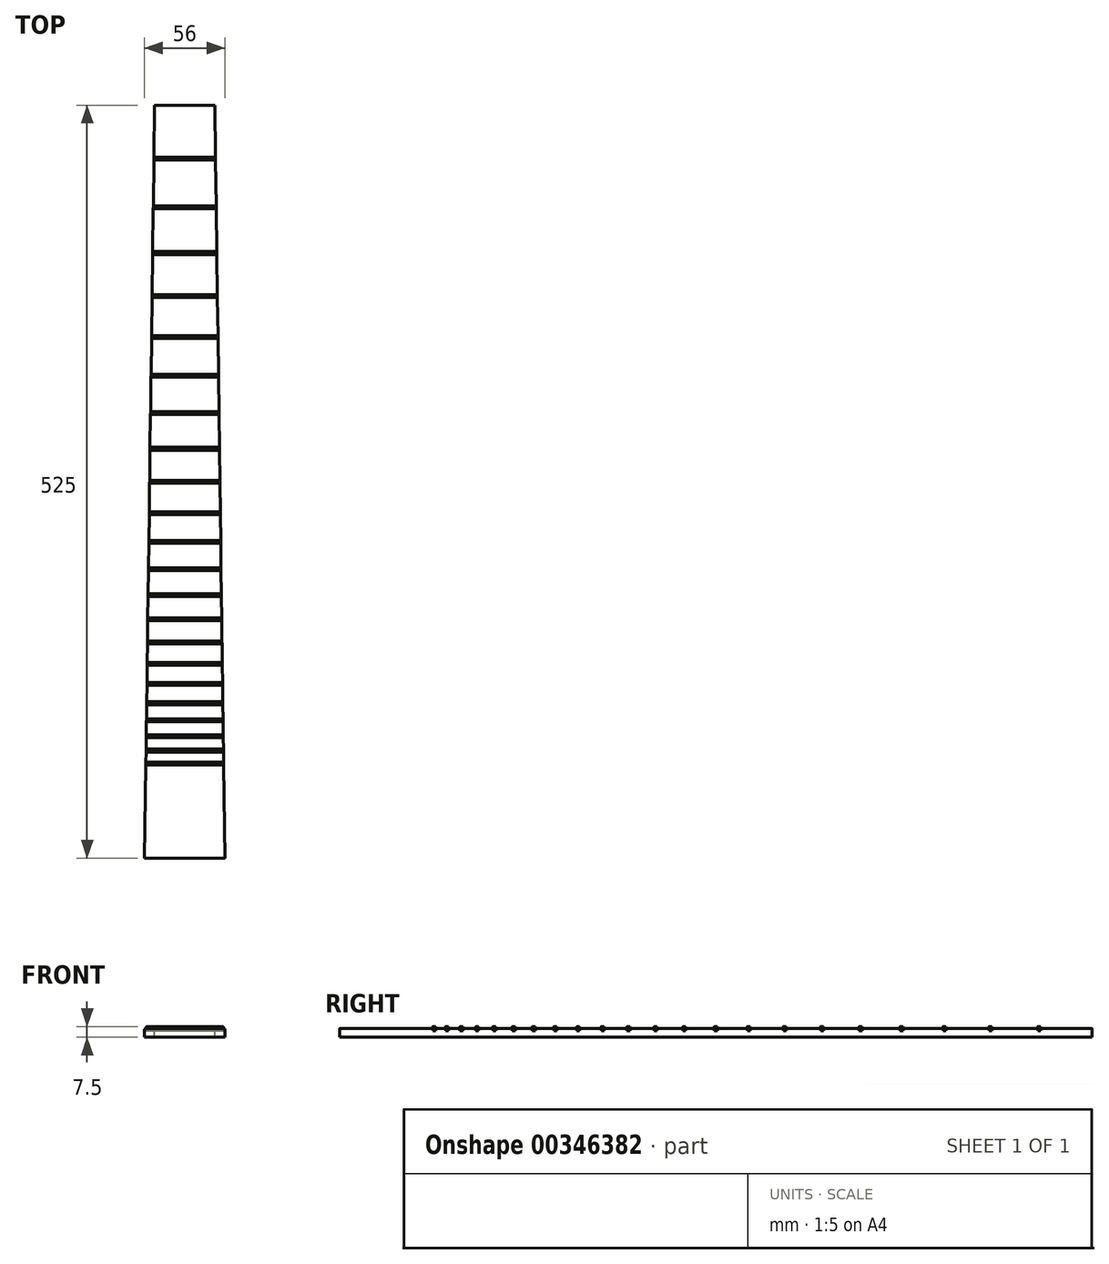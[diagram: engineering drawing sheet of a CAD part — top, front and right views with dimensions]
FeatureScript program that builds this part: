
annotation { "Feature Type Name" : "Feature", "Feature Type Description" : "" }
export const myFeature = defineFeature(function(context is Context, id is Id, definition is map)
    precondition{}
    {
        {
            var Q0;
            Q0=qCreatedBy(makeId("Top.planeOp"),FACE);
            var sketch = newSketch(context, id + "F0", { "sketchPlane" : qUnion([Q0])});
            skLineSegment(sketch, "E0", {"start": v(0, 0) * mm, "end": v(0, 525) * mm, "construction": true});
            skLineSegment(sketch, "E1", {"start": v(0, 525) * mm, "end": v(-21, 525) * mm});
            skLineSegment(sketch, "E2", {"start": v(0, 0) * mm, "end": v(-28, 0) * mm});
            skLineSegment(sketch, "E3", {"start": v(-28, 0) * mm, "end": v(-21, 525) * mm});
            skLineSegment(sketch, "E4", {"start": v(-21.48, 489) * mm, "end": v(0, 489) * mm});
            skLineSegment(sketch, "E5", {"start": v(-21.5, 487) * mm, "end": v(0, 487) * mm});
            skLineSegment(sketch, "E6", {"start": v(-21.93, 455) * mm, "end": v(0, 455) * mm});
            skLineSegment(sketch, "E7", {"start": v(-21.96, 453) * mm, "end": v(0, 453) * mm});
            skLineSegment(sketch, "E8", {"start": v(-22.36, 423) * mm, "end": v(0, 423) * mm});
            skLineSegment(sketch, "E9", {"start": v(-22.39, 421) * mm, "end": v(0, 421) * mm});
            skLineSegment(sketch, "E10", {"start": v(-22.76, 393) * mm, "end": v(0, 393) * mm});
            skLineSegment(sketch, "E11", {"start": v(-22.79, 391) * mm, "end": v(0, 391) * mm});
            skLineSegment(sketch, "E12", {"start": v(-23.14, 364.5) * mm, "end": v(0, 364.5) * mm});
            skLineSegment(sketch, "E13", {"start": v(-23.17, 362.5) * mm, "end": v(0, 362.5) * mm});
            skLineSegment(sketch, "E14", {"start": v(-23.5, 337.5) * mm, "end": v(0, 337.5) * mm});
            skLineSegment(sketch, "E15", {"start": v(-23.53, 335.5) * mm, "end": v(0, 335.5) * mm});
            skLineSegment(sketch, "E16", {"start": v(-23.85, 311.5) * mm, "end": v(0, 311.5) * mm});
            skLineSegment(sketch, "E17", {"start": v(-23.87, 309.5) * mm, "end": v(0, 309.5) * mm});
            skLineSegment(sketch, "E18", {"start": v(-24.18, 286.5) * mm, "end": v(0, 286.5) * mm});
            skLineSegment(sketch, "E19", {"start": v(-24.2, 284.5) * mm, "end": v(0, 284.5) * mm});
            skLineSegment(sketch, "E20", {"start": v(-24.49, 263.5) * mm, "end": v(0, 263.5) * mm});
            skLineSegment(sketch, "E21", {"start": v(-24.51, 261.5) * mm, "end": v(0, 261.5) * mm});
            skLineSegment(sketch, "E22", {"start": v(-24.78, 241.5) * mm, "end": v(0, 241.5) * mm});
            skLineSegment(sketch, "E23", {"start": v(-24.8, 239.5) * mm, "end": v(0, 239.5) * mm});
            skLineSegment(sketch, "E24", {"start": v(-25.05, 221.5) * mm, "end": v(0, 221.5) * mm});
            skLineSegment(sketch, "E25", {"start": v(-25.07, 219.5) * mm, "end": v(0, 219.5) * mm});
            skLineSegment(sketch, "E26", {"start": v(-25.3, 202.5) * mm, "end": v(0, 202.5) * mm});
            skLineSegment(sketch, "E27", {"start": v(-25.33, 200.5) * mm, "end": v(0, 200.5) * mm});
            skLineSegment(sketch, "E28", {"start": v(-25.54, 184.5) * mm, "end": v(0, 184.5) * mm});
            skLineSegment(sketch, "E29", {"start": v(-25.57, 182.5) * mm, "end": v(0, 182.5) * mm});
            skLineSegment(sketch, "E30", {"start": v(-25.77, 167.5) * mm, "end": v(0, 167.5) * mm});
            skLineSegment(sketch, "E31", {"start": v(-25.8, 165.5) * mm, "end": v(0, 165.5) * mm});
            skLineSegment(sketch, "E32", {"start": v(-25.98, 151.5) * mm, "end": v(0, 151.5) * mm});
            skLineSegment(sketch, "E33", {"start": v(-26, 149.5) * mm, "end": v(0, 149.5) * mm});
            skLineSegment(sketch, "E34", {"start": v(-26.18, 136.5) * mm, "end": v(0, 136.5) * mm});
            skLineSegment(sketch, "E35", {"start": v(-26.2, 134.5) * mm, "end": v(0, 134.5) * mm});
            skLineSegment(sketch, "E36", {"start": v(-26.37, 122.5) * mm, "end": v(0, 122.5) * mm});
            skLineSegment(sketch, "E37", {"start": v(-26.4, 120.5) * mm, "end": v(0, 120.5) * mm});
            skLineSegment(sketch, "E38", {"start": v(-26.55, 109) * mm, "end": v(0, 109) * mm});
            skLineSegment(sketch, "E39", {"start": v(-26.57, 107) * mm, "end": v(0, 107) * mm});
            skLineSegment(sketch, "E40", {"start": v(-26.7, 97) * mm, "end": v(0, 97) * mm});
            skLineSegment(sketch, "E41", {"start": v(-26.73, 95) * mm, "end": v(0, 95) * mm});
            skLineSegment(sketch, "E42", {"start": v(-26.85, 86) * mm, "end": v(0, 86) * mm});
            skLineSegment(sketch, "E43", {"start": v(-26.88, 84) * mm, "end": v(0, 84) * mm});
            skLineSegment(sketch, "E44", {"start": v(-26.99, 76) * mm, "end": v(0, 76) * mm});
            skLineSegment(sketch, "E45", {"start": v(-27.01, 74) * mm, "end": v(0, 74) * mm});
            skLineSegment(sketch, "E46", {"start": v(-27.1, 67) * mm, "end": v(0, 67) * mm});
            skLineSegment(sketch, "E47", {"start": v(-27.13, 65) * mm, "end": v(0, 65) * mm});
            skLineSegment(sketch, "E48.MirrorCS", {"start": v(21, 525) * mm, "end": v(0, 525) * mm});
            skLineSegment(sketch, "E49.MirrorCS", {"start": v(28, 0) * mm, "end": v(21, 525) * mm});
            skLineSegment(sketch, "E50.MirrorCS", {"start": v(21.48, 489) * mm, "end": v(0, 489) * mm});
            skLineSegment(sketch, "E51.MirrorCS", {"start": v(21.5, 487) * mm, "end": v(0, 487) * mm});
            skLineSegment(sketch, "E52.MirrorCS", {"start": v(21.93, 455) * mm, "end": v(0, 455) * mm});
            skLineSegment(sketch, "E53.MirrorCS", {"start": v(21.96, 453) * mm, "end": v(0, 453) * mm});
            skLineSegment(sketch, "E54.MirrorCS", {"start": v(22.36, 423) * mm, "end": v(0, 423) * mm});
            skLineSegment(sketch, "E55.MirrorCS", {"start": v(22.39, 421) * mm, "end": v(0, 421) * mm});
            skLineSegment(sketch, "E56.MirrorCS", {"start": v(22.76, 393) * mm, "end": v(0, 393) * mm});
            skLineSegment(sketch, "E57.MirrorCS", {"start": v(22.79, 391) * mm, "end": v(0, 391) * mm});
            skLineSegment(sketch, "E58.MirrorCS", {"start": v(23.14, 364.5) * mm, "end": v(0, 364.5) * mm});
            skLineSegment(sketch, "E59.MirrorCS", {"start": v(23.17, 362.5) * mm, "end": v(0, 362.5) * mm});
            skLineSegment(sketch, "E60.MirrorCS", {"start": v(23.5, 337.5) * mm, "end": v(0, 337.5) * mm});
            skLineSegment(sketch, "E61.MirrorCS", {"start": v(23.53, 335.5) * mm, "end": v(0, 335.5) * mm});
            skLineSegment(sketch, "E62.MirrorCS", {"start": v(23.85, 311.5) * mm, "end": v(0, 311.5) * mm});
            skLineSegment(sketch, "E63.MirrorCS", {"start": v(23.87, 309.5) * mm, "end": v(0, 309.5) * mm});
            skLineSegment(sketch, "E64.MirrorCS", {"start": v(24.18, 286.5) * mm, "end": v(0, 286.5) * mm});
            skLineSegment(sketch, "E65.MirrorCS", {"start": v(24.2, 284.5) * mm, "end": v(0, 284.5) * mm});
            skLineSegment(sketch, "E66.MirrorCS", {"start": v(24.49, 263.5) * mm, "end": v(0, 263.5) * mm});
            skLineSegment(sketch, "E67.MirrorCS", {"start": v(24.51, 261.5) * mm, "end": v(0, 261.5) * mm});
            skLineSegment(sketch, "E68.MirrorCS", {"start": v(24.78, 241.5) * mm, "end": v(0, 241.5) * mm});
            skLineSegment(sketch, "E69.MirrorCS", {"start": v(24.8, 239.5) * mm, "end": v(0, 239.5) * mm});
            skLineSegment(sketch, "E70.MirrorCS", {"start": v(25.05, 221.5) * mm, "end": v(0, 221.5) * mm});
            skLineSegment(sketch, "E71.MirrorCS", {"start": v(25.07, 219.5) * mm, "end": v(0, 219.5) * mm});
            skLineSegment(sketch, "E72.MirrorCS", {"start": v(25.3, 202.5) * mm, "end": v(0, 202.5) * mm});
            skLineSegment(sketch, "E73.MirrorCS", {"start": v(25.33, 200.5) * mm, "end": v(0, 200.5) * mm});
            skLineSegment(sketch, "E74.MirrorCS", {"start": v(25.54, 184.5) * mm, "end": v(0, 184.5) * mm});
            skLineSegment(sketch, "E75.MirrorCS", {"start": v(25.57, 182.5) * mm, "end": v(0, 182.5) * mm});
            skLineSegment(sketch, "E76.MirrorCS", {"start": v(25.77, 167.5) * mm, "end": v(0, 167.5) * mm});
            skLineSegment(sketch, "E77.MirrorCS", {"start": v(25.8, 165.5) * mm, "end": v(0, 165.5) * mm});
            skLineSegment(sketch, "E78.MirrorCS", {"start": v(25.98, 151.5) * mm, "end": v(0, 151.5) * mm});
            skLineSegment(sketch, "E79.MirrorCS", {"start": v(26, 149.5) * mm, "end": v(0, 149.5) * mm});
            skLineSegment(sketch, "E80.MirrorCS", {"start": v(26.18, 136.5) * mm, "end": v(0, 136.5) * mm});
            skLineSegment(sketch, "E81.MirrorCS", {"start": v(26.2, 134.5) * mm, "end": v(0, 134.5) * mm});
            skLineSegment(sketch, "E82.MirrorCS", {"start": v(26.37, 122.5) * mm, "end": v(0, 122.5) * mm});
            skLineSegment(sketch, "E83.MirrorCS", {"start": v(26.4, 120.5) * mm, "end": v(0, 120.5) * mm});
            skLineSegment(sketch, "E84.MirrorCS", {"start": v(26.55, 109) * mm, "end": v(0, 109) * mm});
            skLineSegment(sketch, "E85.MirrorCS", {"start": v(26.57, 107) * mm, "end": v(0, 107) * mm});
            skLineSegment(sketch, "E86.MirrorCS", {"start": v(26.7, 97) * mm, "end": v(0, 97) * mm});
            skLineSegment(sketch, "E87.MirrorCS", {"start": v(26.73, 95) * mm, "end": v(0, 95) * mm});
            skLineSegment(sketch, "E88.MirrorCS", {"start": v(26.85, 86) * mm, "end": v(0, 86) * mm});
            skLineSegment(sketch, "E89.MirrorCS", {"start": v(26.88, 84) * mm, "end": v(0, 84) * mm});
            skLineSegment(sketch, "E90.MirrorCS", {"start": v(26.99, 76) * mm, "end": v(0, 76) * mm});
            skLineSegment(sketch, "E91.MirrorCS", {"start": v(27.01, 74) * mm, "end": v(0, 74) * mm});
            skLineSegment(sketch, "E92.MirrorCS", {"start": v(0, 0) * mm, "end": v(28, 0) * mm});
            skLineSegment(sketch, "E93.MirrorCS", {"start": v(27.1, 67) * mm, "end": v(0, 67) * mm});
            skLineSegment(sketch, "E94.MirrorCS", {"start": v(27.13, 65) * mm, "end": v(0, 65) * mm});
            skSolve(sketch);
        }
        {
            var Q0;
            Q0=qSketchRegion(id+"F0",true);
            extrude(context, id + "F1", {"entities" : qUnion([Q0]), "oppositeDirection" : true, "depth" : 6 * mm});
        }
        {
            var Q0;
            {var subQ1=sQuery(id+"F0.wireOp",EDGE,"E4");Q0=makeQuery(id+"F0.imprint","IMPRINT",FACE,{"disambiguationData":[TD([[makeQuery(id+"F0.imprint","IMPRINT",EDGE,{"derivedFrom":subQ1}),-1.0]])]});}
            var Q1;
            {var subQ1=sQuery(id+"F0.wireOp",EDGE,"E6");Q1=makeQuery(id+"F0.imprint","IMPRINT",FACE,{"disambiguationData":[TD([[makeQuery(id+"F0.imprint","IMPRINT",EDGE,{"derivedFrom":subQ1}),-1.0]])]});}
            var Q2;
            {var subQ1=sQuery(id+"F0.wireOp",EDGE,"E8");Q2=makeQuery(id+"F0.imprint","IMPRINT",FACE,{"disambiguationData":[TD([[makeQuery(id+"F0.imprint","IMPRINT",EDGE,{"derivedFrom":subQ1}),-1.0]])]});}
            var Q3;
            {var subQ0=sQuery(id+"F0.wireOp",EDGE,"E10");Q3=makeQuery(id+"F0.imprint","IMPRINT",FACE,{"disambiguationData":[TD([[makeQuery(id+"F0.imprint","IMPRINT",EDGE,{"derivedFrom":subQ0}),-1.0]])]});}
            var Q4;
            {var subQ1=sQuery(id+"F0.wireOp",EDGE,"E12");Q4=makeQuery(id+"F0.imprint","IMPRINT",FACE,{"disambiguationData":[TD([[makeQuery(id+"F0.imprint","IMPRINT",EDGE,{"derivedFrom":subQ1}),-1.0]])]});}
            var Q5;
            {var subQ1=sQuery(id+"F0.wireOp",EDGE,"E14");Q5=makeQuery(id+"F0.imprint","IMPRINT",FACE,{"disambiguationData":[TD([[makeQuery(id+"F0.imprint","IMPRINT",EDGE,{"derivedFrom":subQ1}),-1.0]])]});}
            var Q6;
            {var subQ1=sQuery(id+"F0.wireOp",EDGE,"E16");Q6=makeQuery(id+"F0.imprint","IMPRINT",FACE,{"disambiguationData":[TD([[makeQuery(id+"F0.imprint","IMPRINT",EDGE,{"derivedFrom":subQ1}),-1.0]])]});}
            var Q7;
            {var subQ4=sQuery(id+"F0.wireOp",EDGE,"E18");Q7=makeQuery(id+"F0.imprint","IMPRINT",FACE,{"disambiguationData":[TD([[makeQuery(id+"F0.imprint","IMPRINT",EDGE,{"derivedFrom":subQ4}),-1.0]])]});}
            var Q8;
            {var subQ0=sQuery(id+"F0.wireOp",EDGE,"E20");Q8=makeQuery(id+"F0.imprint","IMPRINT",FACE,{"disambiguationData":[TD([[makeQuery(id+"F0.imprint","IMPRINT",EDGE,{"derivedFrom":subQ0}),-1.0]])]});}
            var Q9;
            {var subQ1=sQuery(id+"F0.wireOp",EDGE,"E22");Q9=makeQuery(id+"F0.imprint","IMPRINT",FACE,{"disambiguationData":[TD([[makeQuery(id+"F0.imprint","IMPRINT",EDGE,{"derivedFrom":subQ1}),-1.0]])]});}
            var Q10;
            {var subQ1=sQuery(id+"F0.wireOp",EDGE,"E24");Q10=makeQuery(id+"F0.imprint","IMPRINT",FACE,{"disambiguationData":[TD([[makeQuery(id+"F0.imprint","IMPRINT",EDGE,{"derivedFrom":subQ1}),-1.0]])]});}
            var Q11;
            {var subQ1=sQuery(id+"F0.wireOp",EDGE,"E26");Q11=makeQuery(id+"F0.imprint","IMPRINT",FACE,{"disambiguationData":[TD([[makeQuery(id+"F0.imprint","IMPRINT",EDGE,{"derivedFrom":subQ1}),-1.0]])]});}
            var Q12;
            {var subQ4=sQuery(id+"F0.wireOp",EDGE,"E28");Q12=makeQuery(id+"F0.imprint","IMPRINT",FACE,{"disambiguationData":[TD([[makeQuery(id+"F0.imprint","IMPRINT",EDGE,{"derivedFrom":subQ4}),-1.0]])]});}
            var Q13;
            {var subQ0=sQuery(id+"F0.wireOp",EDGE,"E30");Q13=makeQuery(id+"F0.imprint","IMPRINT",FACE,{"disambiguationData":[TD([[makeQuery(id+"F0.imprint","IMPRINT",EDGE,{"derivedFrom":subQ0}),-1.0]])]});}
            var Q14;
            {var subQ1=sQuery(id+"F0.wireOp",EDGE,"E32");Q14=makeQuery(id+"F0.imprint","IMPRINT",FACE,{"disambiguationData":[TD([[makeQuery(id+"F0.imprint","IMPRINT",EDGE,{"derivedFrom":subQ1}),-1.0]])]});}
            var Q15;
            {var subQ1=sQuery(id+"F0.wireOp",EDGE,"E34");Q15=makeQuery(id+"F0.imprint","IMPRINT",FACE,{"disambiguationData":[TD([[makeQuery(id+"F0.imprint","IMPRINT",EDGE,{"derivedFrom":subQ1}),-1.0]])]});}
            var Q16;
            {var subQ1=sQuery(id+"F0.wireOp",EDGE,"E36");Q16=makeQuery(id+"F0.imprint","IMPRINT",FACE,{"disambiguationData":[TD([[makeQuery(id+"F0.imprint","IMPRINT",EDGE,{"derivedFrom":subQ1}),-1.0]])]});}
            var Q17;
            {var subQ4=sQuery(id+"F0.wireOp",EDGE,"E38");Q17=makeQuery(id+"F0.imprint","IMPRINT",FACE,{"disambiguationData":[TD([[makeQuery(id+"F0.imprint","IMPRINT",EDGE,{"derivedFrom":subQ4}),-1.0]])]});}
            var Q18;
            {var subQ0=sQuery(id+"F0.wireOp",EDGE,"E40");Q18=makeQuery(id+"F0.imprint","IMPRINT",FACE,{"disambiguationData":[TD([[makeQuery(id+"F0.imprint","IMPRINT",EDGE,{"derivedFrom":subQ0}),-1.0]])]});}
            var Q19;
            {var subQ1=sQuery(id+"F0.wireOp",EDGE,"E46");Q19=makeQuery(id+"F0.imprint","IMPRINT",FACE,{"disambiguationData":[TD([[makeQuery(id+"F0.imprint","IMPRINT",EDGE,{"derivedFrom":subQ1}),-1.0]])]});}
            var Q20;
            {var subQ1=sQuery(id+"F0.wireOp",EDGE,"E44");Q20=makeQuery(id+"F0.imprint","IMPRINT",FACE,{"disambiguationData":[TD([[makeQuery(id+"F0.imprint","IMPRINT",EDGE,{"derivedFrom":subQ1}),-1.0]])]});}
            var Q21;
            {var subQ4=sQuery(id+"F0.wireOp",EDGE,"E42");Q21=makeQuery(id+"F0.imprint","IMPRINT",FACE,{"disambiguationData":[TD([[makeQuery(id+"F0.imprint","IMPRINT",EDGE,{"derivedFrom":subQ4}),-1.0]])]});}
            extrude(context, id + "F2", {"entities" : qUnion([Q0, Q1, Q2, Q3, Q4, Q5, Q6, Q7, Q8, Q9, Q10, Q11, Q12, Q13, Q14, Q15, Q16, Q17, Q18, Q19, Q20, Q21]), "endBound" : BoundingType.SYMMETRIC, "depth" : 3 * mm});
        }
        {
            var Q0;
            Q0=makeQuery(id+"F1.opExtrude","CAP_EDGE",EDGE,{"disambiguationData":[OSD([sQuery(id+"F0.wireOp",EDGE,"E3")])],"isStart":true});
            var Q1;
            Q1=makeQuery(id+"F1.opExtrude","CAP_EDGE",EDGE,{"disambiguationData":[OSD([sQuery(id+"F0.wireOp",EDGE,"E49.MirrorCS")])],"isStart":true});
            fillet(context, id + "F3", {"entities" : qUnion([Q0, Q1]), "radius" : 0.5 * mm, "tangentPropagation" : true, "allowEdgeOverflow" : false});
        }
        {
            var Q0;
            Q0=makeQuery(id+"F2.opExtrude","SWEPT_BODY",BODY,{"disambiguationData":[OSD([sQuery(id+"F0.wireOp",EDGE,"E3"),sQuery(id+"F0.wireOp",EDGE,"E46"),sQuery(id+"F0.wireOp",EDGE,"E47"),sQuery(id+"F0.wireOp",EDGE,"E49.MirrorCS"),sQuery(id+"F0.wireOp",EDGE,"E93.MirrorCS"),sQuery(id+"F0.wireOp",EDGE,"E94.MirrorCS")])]});
            var Q1;
            Q1=makeQuery(id+"F2.opExtrude","SWEPT_BODY",BODY,{"disambiguationData":[OSD([sQuery(id+"F0.wireOp",EDGE,"E3"),sQuery(id+"F0.wireOp",EDGE,"E44"),sQuery(id+"F0.wireOp",EDGE,"E45"),sQuery(id+"F0.wireOp",EDGE,"E49.MirrorCS"),sQuery(id+"F0.wireOp",EDGE,"E90.MirrorCS"),sQuery(id+"F0.wireOp",EDGE,"E91.MirrorCS")])]});
            var Q2;
            Q2=makeQuery(id+"F2.opExtrude","SWEPT_BODY",BODY,{"disambiguationData":[OSD([sQuery(id+"F0.wireOp",EDGE,"E3"),sQuery(id+"F0.wireOp",EDGE,"E42"),sQuery(id+"F0.wireOp",EDGE,"E43"),sQuery(id+"F0.wireOp",EDGE,"E49.MirrorCS"),sQuery(id+"F0.wireOp",EDGE,"E88.MirrorCS"),sQuery(id+"F0.wireOp",EDGE,"E89.MirrorCS")])]});
            var Q3;
            Q3=makeQuery(id+"F2.opExtrude","SWEPT_BODY",BODY,{"disambiguationData":[OSD([sQuery(id+"F0.wireOp",EDGE,"E3"),sQuery(id+"F0.wireOp",EDGE,"E40"),sQuery(id+"F0.wireOp",EDGE,"E41"),sQuery(id+"F0.wireOp",EDGE,"E49.MirrorCS"),sQuery(id+"F0.wireOp",EDGE,"E86.MirrorCS"),sQuery(id+"F0.wireOp",EDGE,"E87.MirrorCS")])]});
            var Q4;
            Q4=makeQuery(id+"F2.opExtrude","SWEPT_BODY",BODY,{"disambiguationData":[OSD([sQuery(id+"F0.wireOp",EDGE,"E3"),sQuery(id+"F0.wireOp",EDGE,"E38"),sQuery(id+"F0.wireOp",EDGE,"E39"),sQuery(id+"F0.wireOp",EDGE,"E49.MirrorCS"),sQuery(id+"F0.wireOp",EDGE,"E84.MirrorCS"),sQuery(id+"F0.wireOp",EDGE,"E85.MirrorCS")])]});
            var Q5;
            Q5=makeQuery(id+"F2.opExtrude","SWEPT_BODY",BODY,{"disambiguationData":[OSD([sQuery(id+"F0.wireOp",EDGE,"E3"),sQuery(id+"F0.wireOp",EDGE,"E36"),sQuery(id+"F0.wireOp",EDGE,"E37"),sQuery(id+"F0.wireOp",EDGE,"E49.MirrorCS"),sQuery(id+"F0.wireOp",EDGE,"E82.MirrorCS"),sQuery(id+"F0.wireOp",EDGE,"E83.MirrorCS")])]});
            var Q6;
            Q6=makeQuery(id+"F2.opExtrude","SWEPT_BODY",BODY,{"disambiguationData":[OSD([sQuery(id+"F0.wireOp",EDGE,"E3"),sQuery(id+"F0.wireOp",EDGE,"E34"),sQuery(id+"F0.wireOp",EDGE,"E35"),sQuery(id+"F0.wireOp",EDGE,"E49.MirrorCS"),sQuery(id+"F0.wireOp",EDGE,"E80.MirrorCS"),sQuery(id+"F0.wireOp",EDGE,"E81.MirrorCS")])]});
            var Q7;
            Q7=makeQuery(id+"F2.opExtrude","SWEPT_BODY",BODY,{"disambiguationData":[OSD([sQuery(id+"F0.wireOp",EDGE,"E3"),sQuery(id+"F0.wireOp",EDGE,"E32"),sQuery(id+"F0.wireOp",EDGE,"E33"),sQuery(id+"F0.wireOp",EDGE,"E49.MirrorCS"),sQuery(id+"F0.wireOp",EDGE,"E78.MirrorCS"),sQuery(id+"F0.wireOp",EDGE,"E79.MirrorCS")])]});
            var Q8;
            Q8=makeQuery(id+"F2.opExtrude","SWEPT_BODY",BODY,{"disambiguationData":[OSD([sQuery(id+"F0.wireOp",EDGE,"E3"),sQuery(id+"F0.wireOp",EDGE,"E30"),sQuery(id+"F0.wireOp",EDGE,"E31"),sQuery(id+"F0.wireOp",EDGE,"E49.MirrorCS"),sQuery(id+"F0.wireOp",EDGE,"E76.MirrorCS"),sQuery(id+"F0.wireOp",EDGE,"E77.MirrorCS")])]});
            var Q9;
            Q9=makeQuery(id+"F2.opExtrude","SWEPT_BODY",BODY,{"disambiguationData":[OSD([sQuery(id+"F0.wireOp",EDGE,"E3"),sQuery(id+"F0.wireOp",EDGE,"E28"),sQuery(id+"F0.wireOp",EDGE,"E29"),sQuery(id+"F0.wireOp",EDGE,"E49.MirrorCS"),sQuery(id+"F0.wireOp",EDGE,"E74.MirrorCS"),sQuery(id+"F0.wireOp",EDGE,"E75.MirrorCS")])]});
            var Q10;
            Q10=makeQuery(id+"F2.opExtrude","SWEPT_BODY",BODY,{"disambiguationData":[OSD([sQuery(id+"F0.wireOp",EDGE,"E3"),sQuery(id+"F0.wireOp",EDGE,"E26"),sQuery(id+"F0.wireOp",EDGE,"E27"),sQuery(id+"F0.wireOp",EDGE,"E49.MirrorCS"),sQuery(id+"F0.wireOp",EDGE,"E72.MirrorCS"),sQuery(id+"F0.wireOp",EDGE,"E73.MirrorCS")])]});
            var Q11;
            Q11=makeQuery(id+"F2.opExtrude","SWEPT_BODY",BODY,{"disambiguationData":[OSD([sQuery(id+"F0.wireOp",EDGE,"E3"),sQuery(id+"F0.wireOp",EDGE,"E24"),sQuery(id+"F0.wireOp",EDGE,"E25"),sQuery(id+"F0.wireOp",EDGE,"E49.MirrorCS"),sQuery(id+"F0.wireOp",EDGE,"E70.MirrorCS"),sQuery(id+"F0.wireOp",EDGE,"E71.MirrorCS")])]});
            var Q12;
            Q12=makeQuery(id+"F2.opExtrude","SWEPT_BODY",BODY,{"disambiguationData":[OSD([sQuery(id+"F0.wireOp",EDGE,"E3"),sQuery(id+"F0.wireOp",EDGE,"E22"),sQuery(id+"F0.wireOp",EDGE,"E23"),sQuery(id+"F0.wireOp",EDGE,"E49.MirrorCS"),sQuery(id+"F0.wireOp",EDGE,"E68.MirrorCS"),sQuery(id+"F0.wireOp",EDGE,"E69.MirrorCS")])]});
            var Q13;
            Q13=makeQuery(id+"F2.opExtrude","SWEPT_BODY",BODY,{"disambiguationData":[OSD([sQuery(id+"F0.wireOp",EDGE,"E3"),sQuery(id+"F0.wireOp",EDGE,"E20"),sQuery(id+"F0.wireOp",EDGE,"E21"),sQuery(id+"F0.wireOp",EDGE,"E49.MirrorCS"),sQuery(id+"F0.wireOp",EDGE,"E66.MirrorCS"),sQuery(id+"F0.wireOp",EDGE,"E67.MirrorCS")])]});
            var Q14;
            Q14=makeQuery(id+"F2.opExtrude","SWEPT_BODY",BODY,{"disambiguationData":[OSD([sQuery(id+"F0.wireOp",EDGE,"E3"),sQuery(id+"F0.wireOp",EDGE,"E18"),sQuery(id+"F0.wireOp",EDGE,"E19"),sQuery(id+"F0.wireOp",EDGE,"E49.MirrorCS"),sQuery(id+"F0.wireOp",EDGE,"E64.MirrorCS"),sQuery(id+"F0.wireOp",EDGE,"E65.MirrorCS")])]});
            var Q15;
            Q15=makeQuery(id+"F2.opExtrude","SWEPT_BODY",BODY,{"disambiguationData":[OSD([sQuery(id+"F0.wireOp",EDGE,"E3"),sQuery(id+"F0.wireOp",EDGE,"E16"),sQuery(id+"F0.wireOp",EDGE,"E17"),sQuery(id+"F0.wireOp",EDGE,"E49.MirrorCS"),sQuery(id+"F0.wireOp",EDGE,"E62.MirrorCS"),sQuery(id+"F0.wireOp",EDGE,"E63.MirrorCS")])]});
            var Q16;
            Q16=makeQuery(id+"F2.opExtrude","SWEPT_BODY",BODY,{"disambiguationData":[OSD([sQuery(id+"F0.wireOp",EDGE,"E3"),sQuery(id+"F0.wireOp",EDGE,"E14"),sQuery(id+"F0.wireOp",EDGE,"E15"),sQuery(id+"F0.wireOp",EDGE,"E49.MirrorCS"),sQuery(id+"F0.wireOp",EDGE,"E60.MirrorCS"),sQuery(id+"F0.wireOp",EDGE,"E61.MirrorCS")])]});
            var Q17;
            Q17=makeQuery(id+"F2.opExtrude","SWEPT_BODY",BODY,{"disambiguationData":[OSD([sQuery(id+"F0.wireOp",EDGE,"E3"),sQuery(id+"F0.wireOp",EDGE,"E12"),sQuery(id+"F0.wireOp",EDGE,"E13"),sQuery(id+"F0.wireOp",EDGE,"E49.MirrorCS"),sQuery(id+"F0.wireOp",EDGE,"E58.MirrorCS"),sQuery(id+"F0.wireOp",EDGE,"E59.MirrorCS")])]});
            var Q18;
            Q18=makeQuery(id+"F2.opExtrude","SWEPT_BODY",BODY,{"disambiguationData":[OSD([sQuery(id+"F0.wireOp",EDGE,"E3"),sQuery(id+"F0.wireOp",EDGE,"E10"),sQuery(id+"F0.wireOp",EDGE,"E11"),sQuery(id+"F0.wireOp",EDGE,"E49.MirrorCS"),sQuery(id+"F0.wireOp",EDGE,"E56.MirrorCS"),sQuery(id+"F0.wireOp",EDGE,"E57.MirrorCS")])]});
            var Q19;
            Q19=makeQuery(id+"F2.opExtrude","SWEPT_BODY",BODY,{"disambiguationData":[OSD([sQuery(id+"F0.wireOp",EDGE,"E3"),sQuery(id+"F0.wireOp",EDGE,"E8"),sQuery(id+"F0.wireOp",EDGE,"E9"),sQuery(id+"F0.wireOp",EDGE,"E49.MirrorCS"),sQuery(id+"F0.wireOp",EDGE,"E54.MirrorCS"),sQuery(id+"F0.wireOp",EDGE,"E55.MirrorCS")])]});
            var Q20;
            Q20=makeQuery(id+"F2.opExtrude","SWEPT_BODY",BODY,{"disambiguationData":[OSD([sQuery(id+"F0.wireOp",EDGE,"E3"),sQuery(id+"F0.wireOp",EDGE,"E6"),sQuery(id+"F0.wireOp",EDGE,"E7"),sQuery(id+"F0.wireOp",EDGE,"E49.MirrorCS"),sQuery(id+"F0.wireOp",EDGE,"E52.MirrorCS"),sQuery(id+"F0.wireOp",EDGE,"E53.MirrorCS")])]});
            var Q21;
            Q21=makeQuery(id+"F2.opExtrude","SWEPT_BODY",BODY,{"disambiguationData":[OSD([sQuery(id+"F0.wireOp",EDGE,"E3"),sQuery(id+"F0.wireOp",EDGE,"E4"),sQuery(id+"F0.wireOp",EDGE,"E5"),sQuery(id+"F0.wireOp",EDGE,"E49.MirrorCS"),sQuery(id+"F0.wireOp",EDGE,"E50.MirrorCS"),sQuery(id+"F0.wireOp",EDGE,"E51.MirrorCS")])]});
            var Q22;
            Q22=makeQuery(id+"F1.opExtrude","SWEPT_BODY",BODY,{"disambiguationData":[OSD([sQuery(id+"F0.wireOp",EDGE,"E1"),sQuery(id+"F0.wireOp",EDGE,"E2"),sQuery(id+"F0.wireOp",EDGE,"E3"),sQuery(id+"F0.wireOp",EDGE,"E48.MirrorCS"),sQuery(id+"F0.wireOp",EDGE,"E49.MirrorCS"),sQuery(id+"F0.wireOp",EDGE,"E92.MirrorCS")])]});
            booleanBodies(context, id + "F4", {"operationType" : BooleanOperationType.SUBTRACTION, "tools" : qUnion([Q0, Q1, Q2, Q3, Q4, Q5, Q6, Q7, Q8, Q9, Q10, Q11, Q12, Q13, Q14, Q15, Q16, Q17, Q18, Q19, Q20, Q21]), "targets" : qUnion([Q22]), "keepTools" : true});
        }
        {
            var Q0;
            {var subQ0=sQuery(id+"F0.wireOp",EDGE,"E3");Q0=makeQuery(id+"F2.opExtrude","CAP_EDGE",EDGE,{"disambiguationData":[OSD([subQ0]),TDD([makeQuery(id+"F0.imprint","IMPRINT",EDGE,{"disambiguationData":[TD([[makeQuery(id+"F0.imprint","INTERSECT",VERTEX,{"derivedFrom":[subQ0,sQuery(id+"F0.wireOp",EDGE,"E4")]}),1.0]])],"derivedFrom":subQ0})])],"isStart":false});}
            var Q1;
            {var subQ0=sQuery(id+"F0.wireOp",EDGE,"E49.MirrorCS");Q1=makeQuery(id+"F2.opExtrude","CAP_EDGE",EDGE,{"disambiguationData":[OSD([subQ0]),TDD([makeQuery(id+"F0.imprint","IMPRINT",EDGE,{"disambiguationData":[TD([[makeQuery(id+"F0.imprint","INTERSECT",VERTEX,{"derivedFrom":[subQ0,sQuery(id+"F0.wireOp",EDGE,"E50.MirrorCS")]}),1.0]])],"derivedFrom":subQ0})])],"isStart":false});}
            var Q2;
            {var subQ0=sQuery(id+"F0.wireOp",EDGE,"E49.MirrorCS");Q2=makeQuery(id+"F2.opExtrude","CAP_EDGE",EDGE,{"disambiguationData":[OSD([subQ0]),TDD([makeQuery(id+"F0.imprint","IMPRINT",EDGE,{"disambiguationData":[TD([[makeQuery(id+"F0.imprint","INTERSECT",VERTEX,{"derivedFrom":[subQ0,sQuery(id+"F0.wireOp",EDGE,"E52.MirrorCS")]}),1.0]])],"derivedFrom":subQ0})])],"isStart":false});}
            var Q3;
            {var subQ0=sQuery(id+"F0.wireOp",EDGE,"E3");Q3=makeQuery(id+"F2.opExtrude","CAP_EDGE",EDGE,{"disambiguationData":[OSD([subQ0]),TDD([makeQuery(id+"F0.imprint","IMPRINT",EDGE,{"disambiguationData":[TD([[makeQuery(id+"F0.imprint","INTERSECT",VERTEX,{"derivedFrom":[subQ0,sQuery(id+"F0.wireOp",EDGE,"E6")]}),1.0]])],"derivedFrom":subQ0})])],"isStart":false});}
            var Q4;
            {var subQ0=sQuery(id+"F0.wireOp",EDGE,"E3");Q4=makeQuery(id+"F2.opExtrude","CAP_EDGE",EDGE,{"disambiguationData":[OSD([subQ0]),TDD([makeQuery(id+"F0.imprint","IMPRINT",EDGE,{"disambiguationData":[TD([[makeQuery(id+"F0.imprint","INTERSECT",VERTEX,{"derivedFrom":[subQ0,sQuery(id+"F0.wireOp",EDGE,"E8")]}),1.0]])],"derivedFrom":subQ0})])],"isStart":false});}
            var Q5;
            {var subQ0=sQuery(id+"F0.wireOp",EDGE,"E49.MirrorCS");Q5=makeQuery(id+"F2.opExtrude","CAP_EDGE",EDGE,{"disambiguationData":[OSD([subQ0]),TDD([makeQuery(id+"F0.imprint","IMPRINT",EDGE,{"disambiguationData":[TD([[makeQuery(id+"F0.imprint","INTERSECT",VERTEX,{"derivedFrom":[subQ0,sQuery(id+"F0.wireOp",EDGE,"E54.MirrorCS")]}),1.0]])],"derivedFrom":subQ0})])],"isStart":false});}
            var Q6;
            {var subQ0=sQuery(id+"F0.wireOp",EDGE,"E3");Q6=makeQuery(id+"F2.opExtrude","CAP_EDGE",EDGE,{"disambiguationData":[OSD([subQ0]),TDD([makeQuery(id+"F0.imprint","IMPRINT",EDGE,{"disambiguationData":[TD([[makeQuery(id+"F0.imprint","INTERSECT",VERTEX,{"derivedFrom":[subQ0,sQuery(id+"F0.wireOp",EDGE,"E10")]}),1.0]])],"derivedFrom":subQ0})])],"isStart":false});}
            var Q7;
            {var subQ0=sQuery(id+"F0.wireOp",EDGE,"E49.MirrorCS");Q7=makeQuery(id+"F2.opExtrude","CAP_EDGE",EDGE,{"disambiguationData":[OSD([subQ0]),TDD([makeQuery(id+"F0.imprint","IMPRINT",EDGE,{"disambiguationData":[TD([[makeQuery(id+"F0.imprint","INTERSECT",VERTEX,{"derivedFrom":[subQ0,sQuery(id+"F0.wireOp",EDGE,"E56.MirrorCS")]}),1.0]])],"derivedFrom":subQ0})])],"isStart":false});}
            var Q8;
            {var subQ0=sQuery(id+"F0.wireOp",EDGE,"E49.MirrorCS");Q8=makeQuery(id+"F2.opExtrude","CAP_EDGE",EDGE,{"disambiguationData":[OSD([subQ0]),TDD([makeQuery(id+"F0.imprint","IMPRINT",EDGE,{"disambiguationData":[TD([[makeQuery(id+"F0.imprint","INTERSECT",VERTEX,{"derivedFrom":[subQ0,sQuery(id+"F0.wireOp",EDGE,"E58.MirrorCS")]}),1.0]])],"derivedFrom":subQ0})])],"isStart":false});}
            var Q9;
            {var subQ0=sQuery(id+"F0.wireOp",EDGE,"E3");Q9=makeQuery(id+"F2.opExtrude","CAP_EDGE",EDGE,{"disambiguationData":[OSD([subQ0]),TDD([makeQuery(id+"F0.imprint","IMPRINT",EDGE,{"disambiguationData":[TD([[makeQuery(id+"F0.imprint","INTERSECT",VERTEX,{"derivedFrom":[subQ0,sQuery(id+"F0.wireOp",EDGE,"E12")]}),1.0]])],"derivedFrom":subQ0})])],"isStart":false});}
            var Q10;
            {var subQ0=sQuery(id+"F0.wireOp",EDGE,"E3");Q10=makeQuery(id+"F2.opExtrude","CAP_EDGE",EDGE,{"disambiguationData":[OSD([subQ0]),TDD([makeQuery(id+"F0.imprint","IMPRINT",EDGE,{"disambiguationData":[TD([[makeQuery(id+"F0.imprint","INTERSECT",VERTEX,{"derivedFrom":[subQ0,sQuery(id+"F0.wireOp",EDGE,"E14")]}),1.0]])],"derivedFrom":subQ0})])],"isStart":false});}
            var Q11;
            {var subQ0=sQuery(id+"F0.wireOp",EDGE,"E49.MirrorCS");Q11=makeQuery(id+"F2.opExtrude","CAP_EDGE",EDGE,{"disambiguationData":[OSD([subQ0]),TDD([makeQuery(id+"F0.imprint","IMPRINT",EDGE,{"disambiguationData":[TD([[makeQuery(id+"F0.imprint","INTERSECT",VERTEX,{"derivedFrom":[subQ0,sQuery(id+"F0.wireOp",EDGE,"E60.MirrorCS")]}),1.0]])],"derivedFrom":subQ0})])],"isStart":false});}
            var Q12;
            {var subQ0=sQuery(id+"F0.wireOp",EDGE,"E49.MirrorCS");Q12=makeQuery(id+"F2.opExtrude","CAP_EDGE",EDGE,{"disambiguationData":[OSD([subQ0]),TDD([makeQuery(id+"F0.imprint","IMPRINT",EDGE,{"disambiguationData":[TD([[makeQuery(id+"F0.imprint","INTERSECT",VERTEX,{"derivedFrom":[subQ0,sQuery(id+"F0.wireOp",EDGE,"E62.MirrorCS")]}),1.0]])],"derivedFrom":subQ0})])],"isStart":false});}
            var Q13;
            {var subQ0=sQuery(id+"F0.wireOp",EDGE,"E3");Q13=makeQuery(id+"F2.opExtrude","CAP_EDGE",EDGE,{"disambiguationData":[OSD([subQ0]),TDD([makeQuery(id+"F0.imprint","IMPRINT",EDGE,{"disambiguationData":[TD([[makeQuery(id+"F0.imprint","INTERSECT",VERTEX,{"derivedFrom":[subQ0,sQuery(id+"F0.wireOp",EDGE,"E16")]}),1.0]])],"derivedFrom":subQ0})])],"isStart":false});}
            var Q14;
            {var subQ0=sQuery(id+"F0.wireOp",EDGE,"E3");Q14=makeQuery(id+"F2.opExtrude","CAP_EDGE",EDGE,{"disambiguationData":[OSD([subQ0]),TDD([makeQuery(id+"F0.imprint","IMPRINT",EDGE,{"disambiguationData":[TD([[makeQuery(id+"F0.imprint","INTERSECT",VERTEX,{"derivedFrom":[subQ0,sQuery(id+"F0.wireOp",EDGE,"E18")]}),1.0]])],"derivedFrom":subQ0})])],"isStart":false});}
            var Q15;
            {var subQ0=sQuery(id+"F0.wireOp",EDGE,"E49.MirrorCS");Q15=makeQuery(id+"F2.opExtrude","CAP_EDGE",EDGE,{"disambiguationData":[OSD([subQ0]),TDD([makeQuery(id+"F0.imprint","IMPRINT",EDGE,{"disambiguationData":[TD([[makeQuery(id+"F0.imprint","INTERSECT",VERTEX,{"derivedFrom":[subQ0,sQuery(id+"F0.wireOp",EDGE,"E64.MirrorCS")]}),1.0]])],"derivedFrom":subQ0})])],"isStart":false});}
            var Q16;
            {var subQ0=sQuery(id+"F0.wireOp",EDGE,"E49.MirrorCS");Q16=makeQuery(id+"F2.opExtrude","CAP_EDGE",EDGE,{"disambiguationData":[OSD([subQ0]),TDD([makeQuery(id+"F0.imprint","IMPRINT",EDGE,{"disambiguationData":[TD([[makeQuery(id+"F0.imprint","INTERSECT",VERTEX,{"derivedFrom":[subQ0,sQuery(id+"F0.wireOp",EDGE,"E66.MirrorCS")]}),1.0]])],"derivedFrom":subQ0})])],"isStart":false});}
            var Q17;
            {var subQ0=sQuery(id+"F0.wireOp",EDGE,"E3");Q17=makeQuery(id+"F2.opExtrude","CAP_EDGE",EDGE,{"disambiguationData":[OSD([subQ0]),TDD([makeQuery(id+"F0.imprint","IMPRINT",EDGE,{"disambiguationData":[TD([[makeQuery(id+"F0.imprint","INTERSECT",VERTEX,{"derivedFrom":[subQ0,sQuery(id+"F0.wireOp",EDGE,"E20")]}),1.0]])],"derivedFrom":subQ0})])],"isStart":false});}
            var Q18;
            {var subQ0=sQuery(id+"F0.wireOp",EDGE,"E3");Q18=makeQuery(id+"F2.opExtrude","CAP_EDGE",EDGE,{"disambiguationData":[OSD([subQ0]),TDD([makeQuery(id+"F0.imprint","IMPRINT",EDGE,{"disambiguationData":[TD([[makeQuery(id+"F0.imprint","INTERSECT",VERTEX,{"derivedFrom":[subQ0,sQuery(id+"F0.wireOp",EDGE,"E22")]}),1.0]])],"derivedFrom":subQ0})])],"isStart":false});}
            var Q19;
            {var subQ0=sQuery(id+"F0.wireOp",EDGE,"E49.MirrorCS");Q19=makeQuery(id+"F2.opExtrude","CAP_EDGE",EDGE,{"disambiguationData":[OSD([subQ0]),TDD([makeQuery(id+"F0.imprint","IMPRINT",EDGE,{"disambiguationData":[TD([[makeQuery(id+"F0.imprint","INTERSECT",VERTEX,{"derivedFrom":[subQ0,sQuery(id+"F0.wireOp",EDGE,"E68.MirrorCS")]}),1.0]])],"derivedFrom":subQ0})])],"isStart":false});}
            var Q20;
            {var subQ0=sQuery(id+"F0.wireOp",EDGE,"E49.MirrorCS");Q20=makeQuery(id+"F2.opExtrude","CAP_EDGE",EDGE,{"disambiguationData":[OSD([subQ0]),TDD([makeQuery(id+"F0.imprint","IMPRINT",EDGE,{"disambiguationData":[TD([[makeQuery(id+"F0.imprint","INTERSECT",VERTEX,{"derivedFrom":[subQ0,sQuery(id+"F0.wireOp",EDGE,"E70.MirrorCS")]}),1.0]])],"derivedFrom":subQ0})])],"isStart":false});}
            var Q21;
            {var subQ0=sQuery(id+"F0.wireOp",EDGE,"E3");Q21=makeQuery(id+"F2.opExtrude","CAP_EDGE",EDGE,{"disambiguationData":[OSD([subQ0]),TDD([makeQuery(id+"F0.imprint","IMPRINT",EDGE,{"disambiguationData":[TD([[makeQuery(id+"F0.imprint","INTERSECT",VERTEX,{"derivedFrom":[subQ0,sQuery(id+"F0.wireOp",EDGE,"E24")]}),1.0]])],"derivedFrom":subQ0})])],"isStart":false});}
            var Q22;
            {var subQ0=sQuery(id+"F0.wireOp",EDGE,"E3");Q22=makeQuery(id+"F2.opExtrude","CAP_EDGE",EDGE,{"disambiguationData":[OSD([subQ0]),TDD([makeQuery(id+"F0.imprint","IMPRINT",EDGE,{"disambiguationData":[TD([[makeQuery(id+"F0.imprint","INTERSECT",VERTEX,{"derivedFrom":[subQ0,sQuery(id+"F0.wireOp",EDGE,"E26")]}),1.0]])],"derivedFrom":subQ0})])],"isStart":false});}
            var Q23;
            {var subQ0=sQuery(id+"F0.wireOp",EDGE,"E49.MirrorCS");Q23=makeQuery(id+"F2.opExtrude","CAP_EDGE",EDGE,{"disambiguationData":[OSD([subQ0]),TDD([makeQuery(id+"F0.imprint","IMPRINT",EDGE,{"disambiguationData":[TD([[makeQuery(id+"F0.imprint","INTERSECT",VERTEX,{"derivedFrom":[subQ0,sQuery(id+"F0.wireOp",EDGE,"E72.MirrorCS")]}),1.0]])],"derivedFrom":subQ0})])],"isStart":false});}
            var Q24;
            {var subQ0=sQuery(id+"F0.wireOp",EDGE,"E3");Q24=makeQuery(id+"F2.opExtrude","CAP_EDGE",EDGE,{"disambiguationData":[OSD([subQ0]),TDD([makeQuery(id+"F0.imprint","IMPRINT",EDGE,{"disambiguationData":[TD([[makeQuery(id+"F0.imprint","INTERSECT",VERTEX,{"derivedFrom":[subQ0,sQuery(id+"F0.wireOp",EDGE,"E28")]}),1.0]])],"derivedFrom":subQ0})])],"isStart":false});}
            var Q25;
            {var subQ0=sQuery(id+"F0.wireOp",EDGE,"E49.MirrorCS");Q25=makeQuery(id+"F2.opExtrude","CAP_EDGE",EDGE,{"disambiguationData":[OSD([subQ0]),TDD([makeQuery(id+"F0.imprint","IMPRINT",EDGE,{"disambiguationData":[TD([[makeQuery(id+"F0.imprint","INTERSECT",VERTEX,{"derivedFrom":[subQ0,sQuery(id+"F0.wireOp",EDGE,"E74.MirrorCS")]}),1.0]])],"derivedFrom":subQ0})])],"isStart":false});}
            var Q26;
            {var subQ0=sQuery(id+"F0.wireOp",EDGE,"E49.MirrorCS");Q26=makeQuery(id+"F2.opExtrude","CAP_EDGE",EDGE,{"disambiguationData":[OSD([subQ0]),TDD([makeQuery(id+"F0.imprint","IMPRINT",EDGE,{"disambiguationData":[TD([[makeQuery(id+"F0.imprint","INTERSECT",VERTEX,{"derivedFrom":[subQ0,sQuery(id+"F0.wireOp",EDGE,"E76.MirrorCS")]}),1.0]])],"derivedFrom":subQ0})])],"isStart":false});}
            var Q27;
            {var subQ0=sQuery(id+"F0.wireOp",EDGE,"E3");Q27=makeQuery(id+"F2.opExtrude","CAP_EDGE",EDGE,{"disambiguationData":[OSD([subQ0]),TDD([makeQuery(id+"F0.imprint","IMPRINT",EDGE,{"disambiguationData":[TD([[makeQuery(id+"F0.imprint","INTERSECT",VERTEX,{"derivedFrom":[subQ0,sQuery(id+"F0.wireOp",EDGE,"E30")]}),1.0]])],"derivedFrom":subQ0})])],"isStart":false});}
            var Q28;
            {var subQ0=sQuery(id+"F0.wireOp",EDGE,"E3");Q28=makeQuery(id+"F2.opExtrude","CAP_EDGE",EDGE,{"disambiguationData":[OSD([subQ0]),TDD([makeQuery(id+"F0.imprint","IMPRINT",EDGE,{"disambiguationData":[TD([[makeQuery(id+"F0.imprint","INTERSECT",VERTEX,{"derivedFrom":[subQ0,sQuery(id+"F0.wireOp",EDGE,"E32")]}),1.0]])],"derivedFrom":subQ0})])],"isStart":false});}
            var Q29;
            {var subQ0=sQuery(id+"F0.wireOp",EDGE,"E49.MirrorCS");Q29=makeQuery(id+"F2.opExtrude","CAP_EDGE",EDGE,{"disambiguationData":[OSD([subQ0]),TDD([makeQuery(id+"F0.imprint","IMPRINT",EDGE,{"disambiguationData":[TD([[makeQuery(id+"F0.imprint","INTERSECT",VERTEX,{"derivedFrom":[subQ0,sQuery(id+"F0.wireOp",EDGE,"E78.MirrorCS")]}),1.0]])],"derivedFrom":subQ0})])],"isStart":false});}
            var Q30;
            {var subQ0=sQuery(id+"F0.wireOp",EDGE,"E49.MirrorCS");Q30=makeQuery(id+"F2.opExtrude","CAP_EDGE",EDGE,{"disambiguationData":[OSD([subQ0]),TDD([makeQuery(id+"F0.imprint","IMPRINT",EDGE,{"disambiguationData":[TD([[makeQuery(id+"F0.imprint","INTERSECT",VERTEX,{"derivedFrom":[subQ0,sQuery(id+"F0.wireOp",EDGE,"E80.MirrorCS")]}),1.0]])],"derivedFrom":subQ0})])],"isStart":false});}
            var Q31;
            {var subQ0=sQuery(id+"F0.wireOp",EDGE,"E3");Q31=makeQuery(id+"F2.opExtrude","CAP_EDGE",EDGE,{"disambiguationData":[OSD([subQ0]),TDD([makeQuery(id+"F0.imprint","IMPRINT",EDGE,{"disambiguationData":[TD([[makeQuery(id+"F0.imprint","INTERSECT",VERTEX,{"derivedFrom":[subQ0,sQuery(id+"F0.wireOp",EDGE,"E34")]}),1.0]])],"derivedFrom":subQ0})])],"isStart":false});}
            var Q32;
            {var subQ0=sQuery(id+"F0.wireOp",EDGE,"E3");Q32=makeQuery(id+"F2.opExtrude","CAP_EDGE",EDGE,{"disambiguationData":[OSD([subQ0]),TDD([makeQuery(id+"F0.imprint","IMPRINT",EDGE,{"disambiguationData":[TD([[makeQuery(id+"F0.imprint","INTERSECT",VERTEX,{"derivedFrom":[subQ0,sQuery(id+"F0.wireOp",EDGE,"E36")]}),1.0]])],"derivedFrom":subQ0})])],"isStart":false});}
            var Q33;
            {var subQ0=sQuery(id+"F0.wireOp",EDGE,"E49.MirrorCS");Q33=makeQuery(id+"F2.opExtrude","CAP_EDGE",EDGE,{"disambiguationData":[OSD([subQ0]),TDD([makeQuery(id+"F0.imprint","IMPRINT",EDGE,{"disambiguationData":[TD([[makeQuery(id+"F0.imprint","INTERSECT",VERTEX,{"derivedFrom":[subQ0,sQuery(id+"F0.wireOp",EDGE,"E82.MirrorCS")]}),1.0]])],"derivedFrom":subQ0})])],"isStart":false});}
            var Q34;
            {var subQ0=sQuery(id+"F0.wireOp",EDGE,"E49.MirrorCS");Q34=makeQuery(id+"F2.opExtrude","CAP_EDGE",EDGE,{"disambiguationData":[OSD([subQ0]),TDD([makeQuery(id+"F0.imprint","IMPRINT",EDGE,{"disambiguationData":[TD([[makeQuery(id+"F0.imprint","INTERSECT",VERTEX,{"derivedFrom":[subQ0,sQuery(id+"F0.wireOp",EDGE,"E84.MirrorCS")]}),1.0]])],"derivedFrom":subQ0})])],"isStart":false});}
            var Q35;
            {var subQ0=sQuery(id+"F0.wireOp",EDGE,"E3");Q35=makeQuery(id+"F2.opExtrude","CAP_EDGE",EDGE,{"disambiguationData":[OSD([subQ0]),TDD([makeQuery(id+"F0.imprint","IMPRINT",EDGE,{"disambiguationData":[TD([[makeQuery(id+"F0.imprint","INTERSECT",VERTEX,{"derivedFrom":[subQ0,sQuery(id+"F0.wireOp",EDGE,"E38")]}),1.0]])],"derivedFrom":subQ0})])],"isStart":false});}
            var Q36;
            {var subQ0=sQuery(id+"F0.wireOp",EDGE,"E3");Q36=makeQuery(id+"F2.opExtrude","CAP_EDGE",EDGE,{"disambiguationData":[OSD([subQ0]),TDD([makeQuery(id+"F0.imprint","IMPRINT",EDGE,{"disambiguationData":[TD([[makeQuery(id+"F0.imprint","INTERSECT",VERTEX,{"derivedFrom":[subQ0,sQuery(id+"F0.wireOp",EDGE,"E40")]}),1.0]])],"derivedFrom":subQ0})])],"isStart":false});}
            var Q37;
            {var subQ0=sQuery(id+"F0.wireOp",EDGE,"E49.MirrorCS");Q37=makeQuery(id+"F2.opExtrude","CAP_EDGE",EDGE,{"disambiguationData":[OSD([subQ0]),TDD([makeQuery(id+"F0.imprint","IMPRINT",EDGE,{"disambiguationData":[TD([[makeQuery(id+"F0.imprint","INTERSECT",VERTEX,{"derivedFrom":[subQ0,sQuery(id+"F0.wireOp",EDGE,"E86.MirrorCS")]}),1.0]])],"derivedFrom":subQ0})])],"isStart":false});}
            var Q38;
            {var subQ0=sQuery(id+"F0.wireOp",EDGE,"E49.MirrorCS");Q38=makeQuery(id+"F2.opExtrude","CAP_EDGE",EDGE,{"disambiguationData":[OSD([subQ0]),TDD([makeQuery(id+"F0.imprint","IMPRINT",EDGE,{"disambiguationData":[TD([[makeQuery(id+"F0.imprint","INTERSECT",VERTEX,{"derivedFrom":[subQ0,sQuery(id+"F0.wireOp",EDGE,"E88.MirrorCS")]}),1.0]])],"derivedFrom":subQ0})])],"isStart":false});}
            var Q39;
            {var subQ0=sQuery(id+"F0.wireOp",EDGE,"E49.MirrorCS");Q39=makeQuery(id+"F2.opExtrude","CAP_EDGE",EDGE,{"disambiguationData":[OSD([subQ0]),TDD([makeQuery(id+"F0.imprint","IMPRINT",EDGE,{"disambiguationData":[TD([[makeQuery(id+"F0.imprint","INTERSECT",VERTEX,{"derivedFrom":[subQ0,sQuery(id+"F0.wireOp",EDGE,"E90.MirrorCS")]}),1.0]])],"derivedFrom":subQ0})])],"isStart":false});}
            var Q40;
            {var subQ0=sQuery(id+"F0.wireOp",EDGE,"E49.MirrorCS");Q40=makeQuery(id+"F2.opExtrude","CAP_EDGE",EDGE,{"disambiguationData":[OSD([subQ0]),TDD([makeQuery(id+"F0.imprint","IMPRINT",EDGE,{"disambiguationData":[TD([[makeQuery(id+"F0.imprint","INTERSECT",VERTEX,{"derivedFrom":[subQ0,sQuery(id+"F0.wireOp",EDGE,"E93.MirrorCS")]}),1.0]])],"derivedFrom":subQ0})])],"isStart":false});}
            var Q41;
            {var subQ0=sQuery(id+"F0.wireOp",EDGE,"E3");Q41=makeQuery(id+"F2.opExtrude","CAP_EDGE",EDGE,{"disambiguationData":[OSD([subQ0]),TDD([makeQuery(id+"F0.imprint","IMPRINT",EDGE,{"disambiguationData":[TD([[makeQuery(id+"F0.imprint","INTERSECT",VERTEX,{"derivedFrom":[subQ0,sQuery(id+"F0.wireOp",EDGE,"E42")]}),1.0]])],"derivedFrom":subQ0})])],"isStart":false});}
            var Q42;
            {var subQ0=sQuery(id+"F0.wireOp",EDGE,"E3");Q42=makeQuery(id+"F2.opExtrude","CAP_EDGE",EDGE,{"disambiguationData":[OSD([subQ0]),TDD([makeQuery(id+"F0.imprint","IMPRINT",EDGE,{"disambiguationData":[TD([[makeQuery(id+"F0.imprint","INTERSECT",VERTEX,{"derivedFrom":[subQ0,sQuery(id+"F0.wireOp",EDGE,"E46")]}),1.0]])],"derivedFrom":subQ0})])],"isStart":false});}
            var Q43;
            {var subQ0=sQuery(id+"F0.wireOp",EDGE,"E3");Q43=makeQuery(id+"F2.opExtrude","CAP_EDGE",EDGE,{"disambiguationData":[OSD([subQ0]),TDD([makeQuery(id+"F0.imprint","IMPRINT",EDGE,{"disambiguationData":[TD([[makeQuery(id+"F0.imprint","INTERSECT",VERTEX,{"derivedFrom":[subQ0,sQuery(id+"F0.wireOp",EDGE,"E44")]}),1.0]])],"derivedFrom":subQ0})])],"isStart":false});}
            fillet(context, id + "F5", {"entities" : qUnion([Q0, Q1, Q2, Q3, Q4, Q5, Q6, Q7, Q8, Q9, Q10, Q11, Q12, Q13, Q14, Q15, Q16, Q17, Q18, Q19, Q20, Q21, Q22, Q23, Q24, Q25, Q26, Q27, Q28, Q29, Q30, Q31, Q32, Q33, Q34, Q35, Q36, Q37, Q38, Q39, Q40, Q41, Q42, Q43]), "radius" : 1 * mm, "tangentPropagation" : true, "allowEdgeOverflow" : false});
        }
    });
